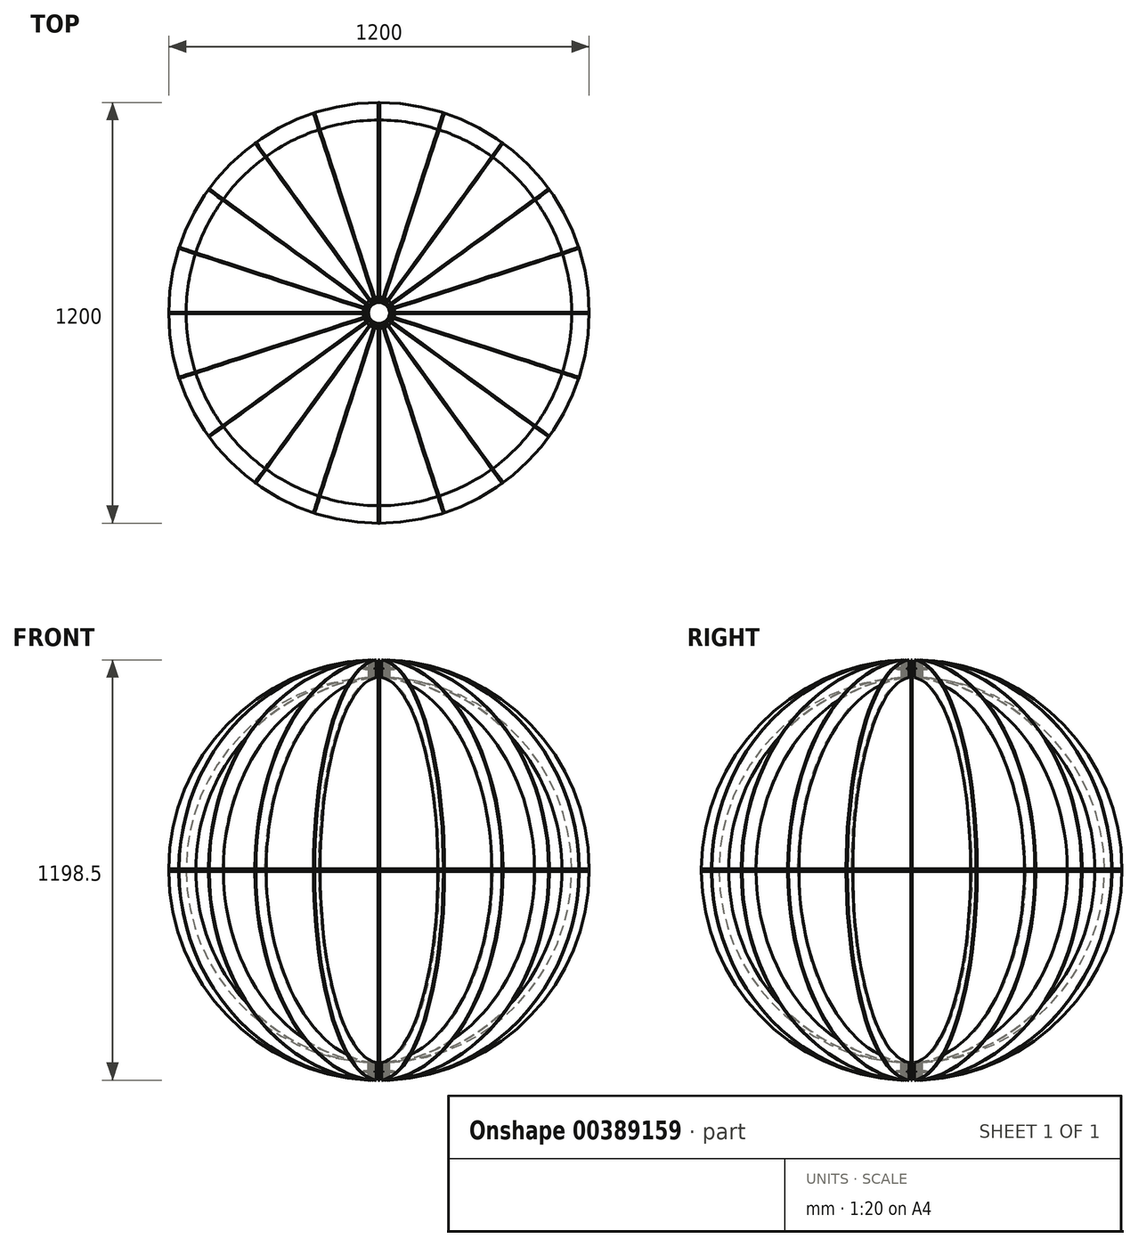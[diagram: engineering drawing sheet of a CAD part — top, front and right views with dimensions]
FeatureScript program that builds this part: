
annotation { "Feature Type Name" : "Feature", "Feature Type Description" : "" }
export const myFeature = defineFeature(function(context is Context, id is Id, definition is map)
    precondition{}
    {
        {
            var Q0;
            Q0=qCreatedBy(makeId("Front.planeOp"),FACE);
            var sketch = newSketch(context, id + "F0", { "sketchPlane" : qUnion([Q0])});
            skArc(sketch, "E0", {"start": v(-600, 0) * mm, "mid": v(-424.26, -424.26) * mm, "end": v(0, -600) * mm});
            skArc(sketch, "E1", {"start": v(-550, 0) * mm, "mid": v(-388.9, -388.9) * mm, "end": v(0, -550) * mm});
            skLineSegment(sketch, "E2", {"start": v(0, 0) * mm, "end": v(0, -799.31) * mm});
            skLineSegment(sketch, "E3", {"start": v(0, 0) * mm, "end": v(-999.51, 0) * mm});
            skLineSegment(sketch, "E4", {"start": v(-631.08, -4) * mm, "end": v(-585, -4) * mm});
            skLineSegment(sketch, "E5", {"start": v(-585, -4) * mm, "end": v(-585, -2) * mm});
            skLineSegment(sketch, "E6", {"start": v(-585, -2) * mm, "end": v(-565, -2) * mm});
            skLineSegment(sketch, "E7", {"start": v(-565, -2) * mm, "end": v(-565, -4) * mm});
            skLineSegment(sketch, "E8", {"start": v(-565, -4) * mm, "end": v(-518.76, -4) * mm});
            skLineSegment(sketch, "E9", {"start": v(-30, -645.62) * mm, "end": v(-30, -482.05) * mm});
            skLineSegment(sketch, "E10", {"start": v(-30, -577.5) * mm, "end": v(-40, -577.5) * mm});
            skLineSegment(sketch, "E11", {"start": v(-40, -577.5) * mm, "end": v(-40, -572.5) * mm});
            skLineSegment(sketch, "E12", {"start": v(-40, -572.5) * mm, "end": v(-30, -572.5) * mm});
            skSolve(sketch);
        }
        {
            var Q0;
            {var subQ12=sQuery(id+"F0.wireOp",EDGE,"E5");Q0=makeQuery(id+"F0.imprint","IMPRINT",FACE,{"disambiguationData":[TD([[makeQuery(id+"F0.imprint","IMPRINT",EDGE,{"derivedFrom":subQ12}),-1.0]])]});}
            extrude(context, id + "F1", {"entities" : qUnion([Q0]), "endBound" : BoundingType.SYMMETRIC, "depth" : 4 * mm});
        }
        {
            var Q0;
            Q0=qCreatedBy(makeId("Front.planeOp"),FACE);
            var sketch = newSketch(context, id + "F2", { "sketchPlane" : qUnion([Q0])});
            skLineSegment(sketch, "E13", {"start": v(0, -374.59) * mm, "end": v(0, 317) * mm});
            skSolve(sketch);
        }
        {
            var Q0;
            Q0=makeQuery(id+"F1.opExtrude","SWEPT_BODY",BODY,{"disambiguationData":[OSD([sQuery(id+"F0.wireOp",EDGE,"E0"),sQuery(id+"F0.wireOp",EDGE,"E1"),sQuery(id+"F0.wireOp",EDGE,"E4"),sQuery(id+"F0.wireOp",EDGE,"E5"),sQuery(id+"F0.wireOp",EDGE,"E6"),sQuery(id+"F0.wireOp",EDGE,"E7"),sQuery(id+"F0.wireOp",EDGE,"E8"),sQuery(id+"F0.wireOp",EDGE,"E9"),sQuery(id+"F0.wireOp",EDGE,"E10"),sQuery(id+"F0.wireOp",EDGE,"E11"),sQuery(id+"F0.wireOp",EDGE,"E12")])]});
            var Q1;
            Q1=sQuery(id+"F2.wireOp",EDGE,"E13");
            circularPattern(context, id + "F3", {"entities" : qUnion([Q0]), "axis" : qUnion([Q1]), "angle" : 360 * degree, "instanceCount" : 20, "equalSpace" : true});
        }
        {
            var Q0;
            Q0=qCreatedBy(makeId("Top.planeOp"),FACE);
            var sketch = newSketch(context, id + "F4", { "sketchPlane" : qUnion([Q0])});
            skLineSegment(sketch, "E14.0.0", {"start": v(-330.48, 458.27) * mm, "end": v(-342.24, 474.45) * mm});
            skLineSegment(sketch, "E14.0.1", {"start": v(-342.24, 474.45) * mm, "end": v(-345.47, 472.1) * mm});
            skLineSegment(sketch, "E14.0.2", {"start": v(-345.47, 472.1) * mm, "end": v(-333.72, 455.92) * mm});
            skLineSegment(sketch, "E14.0.3", {"start": v(-333.72, 455.92) * mm, "end": v(-330.48, 458.27) * mm});
            skLineSegment(sketch, "E15.0.0", {"start": v(-172.7, 537.96) * mm, "end": v(-178.87, 556.99) * mm});
            skLineSegment(sketch, "E15.0.1", {"start": v(-178.87, 556.99) * mm, "end": v(-182.68, 555.75) * mm});
            skLineSegment(sketch, "E15.0.2", {"start": v(-182.68, 555.75) * mm, "end": v(-176.5, 536.73) * mm});
            skLineSegment(sketch, "E15.0.3", {"start": v(-176.5, 536.73) * mm, "end": v(-172.7, 537.96) * mm});
            skLineSegment(sketch, "E16.0.0", {"start": v(2, 565) * mm, "end": v(2, 585) * mm});
            skLineSegment(sketch, "E16.0.1", {"start": v(2, 585) * mm, "end": v(-2, 585) * mm});
            skLineSegment(sketch, "E16.0.2", {"start": v(-2, 585) * mm, "end": v(-2, 565) * mm});
            skLineSegment(sketch, "E16.0.3", {"start": v(-2, 565) * mm, "end": v(2, 565) * mm});
            skLineSegment(sketch, "E17.0.0", {"start": v(176.5, 536.73) * mm, "end": v(182.68, 555.75) * mm});
            skLineSegment(sketch, "E17.0.1", {"start": v(182.68, 555.75) * mm, "end": v(178.87, 556.99) * mm});
            skLineSegment(sketch, "E17.0.2", {"start": v(178.87, 556.99) * mm, "end": v(172.7, 537.96) * mm});
            skLineSegment(sketch, "E17.0.3", {"start": v(172.7, 537.96) * mm, "end": v(176.5, 536.73) * mm});
            skLineSegment(sketch, "E18.0.0", {"start": v(333.72, 455.92) * mm, "end": v(345.47, 472.1) * mm});
            skLineSegment(sketch, "E18.0.1", {"start": v(345.47, 472.1) * mm, "end": v(342.24, 474.45) * mm});
            skLineSegment(sketch, "E18.0.2", {"start": v(342.24, 474.45) * mm, "end": v(330.48, 458.27) * mm});
            skLineSegment(sketch, "E18.0.3", {"start": v(330.48, 458.27) * mm, "end": v(333.72, 455.92) * mm});
            skLineSegment(sketch, "E19.0.0", {"start": v(458.27, 330.48) * mm, "end": v(474.45, 342.24) * mm});
            skLineSegment(sketch, "E19.0.1", {"start": v(474.45, 342.24) * mm, "end": v(472.1, 345.47) * mm});
            skLineSegment(sketch, "E19.0.2", {"start": v(472.1, 345.47) * mm, "end": v(455.92, 333.72) * mm});
            skLineSegment(sketch, "E19.0.3", {"start": v(455.92, 333.72) * mm, "end": v(458.27, 330.48) * mm});
            skLineSegment(sketch, "E20.0.0", {"start": v(537.96, 172.7) * mm, "end": v(556.99, 178.87) * mm});
            skLineSegment(sketch, "E20.0.1", {"start": v(556.99, 178.87) * mm, "end": v(555.75, 182.68) * mm});
            skLineSegment(sketch, "E20.0.2", {"start": v(555.75, 182.68) * mm, "end": v(536.73, 176.5) * mm});
            skLineSegment(sketch, "E20.0.3", {"start": v(536.73, 176.5) * mm, "end": v(537.96, 172.7) * mm});
            skLineSegment(sketch, "E21.0.0", {"start": v(565, -2) * mm, "end": v(585, -2) * mm});
            skLineSegment(sketch, "E21.0.1", {"start": v(585, -2) * mm, "end": v(585, 2) * mm});
            skLineSegment(sketch, "E21.0.2", {"start": v(585, 2) * mm, "end": v(565, 2) * mm});
            skLineSegment(sketch, "E21.0.3", {"start": v(565, 2) * mm, "end": v(565, -2) * mm});
            skLineSegment(sketch, "E22.0.0", {"start": v(536.73, -176.5) * mm, "end": v(555.75, -182.68) * mm});
            skLineSegment(sketch, "E22.0.1", {"start": v(555.75, -182.68) * mm, "end": v(556.99, -178.87) * mm});
            skLineSegment(sketch, "E22.0.2", {"start": v(556.99, -178.87) * mm, "end": v(537.96, -172.7) * mm});
            skLineSegment(sketch, "E22.0.3", {"start": v(537.96, -172.7) * mm, "end": v(536.73, -176.5) * mm});
            skLineSegment(sketch, "E23.0.0", {"start": v(455.92, -333.72) * mm, "end": v(472.1, -345.47) * mm});
            skLineSegment(sketch, "E23.0.1", {"start": v(472.1, -345.47) * mm, "end": v(474.45, -342.24) * mm});
            skLineSegment(sketch, "E23.0.2", {"start": v(474.45, -342.24) * mm, "end": v(458.27, -330.48) * mm});
            skLineSegment(sketch, "E23.0.3", {"start": v(458.27, -330.48) * mm, "end": v(455.92, -333.72) * mm});
            skLineSegment(sketch, "E24.0.0", {"start": v(330.48, -458.27) * mm, "end": v(342.24, -474.45) * mm});
            skLineSegment(sketch, "E24.0.1", {"start": v(342.24, -474.45) * mm, "end": v(345.47, -472.1) * mm});
            skLineSegment(sketch, "E24.0.2", {"start": v(345.47, -472.1) * mm, "end": v(333.72, -455.92) * mm});
            skLineSegment(sketch, "E24.0.3", {"start": v(333.72, -455.92) * mm, "end": v(330.48, -458.27) * mm});
            skLineSegment(sketch, "E25.0.0", {"start": v(172.7, -537.96) * mm, "end": v(178.87, -556.99) * mm});
            skLineSegment(sketch, "E25.0.1", {"start": v(178.87, -556.99) * mm, "end": v(182.68, -555.75) * mm});
            skLineSegment(sketch, "E25.0.2", {"start": v(182.68, -555.75) * mm, "end": v(176.5, -536.73) * mm});
            skLineSegment(sketch, "E25.0.3", {"start": v(176.5, -536.73) * mm, "end": v(172.7, -537.96) * mm});
            skLineSegment(sketch, "E26.0.0", {"start": v(-2, -565) * mm, "end": v(-2, -585) * mm});
            skLineSegment(sketch, "E26.0.1", {"start": v(-2, -585) * mm, "end": v(2, -585) * mm});
            skLineSegment(sketch, "E26.0.2", {"start": v(2, -585) * mm, "end": v(2, -565) * mm});
            skLineSegment(sketch, "E26.0.3", {"start": v(2, -565) * mm, "end": v(-2, -565) * mm});
            skLineSegment(sketch, "E27.0.0", {"start": v(-176.5, -536.73) * mm, "end": v(-182.68, -555.75) * mm});
            skLineSegment(sketch, "E27.0.1", {"start": v(-182.68, -555.75) * mm, "end": v(-178.87, -556.99) * mm});
            skLineSegment(sketch, "E27.0.2", {"start": v(-178.87, -556.99) * mm, "end": v(-172.7, -537.96) * mm});
            skLineSegment(sketch, "E27.0.3", {"start": v(-172.7, -537.96) * mm, "end": v(-176.5, -536.73) * mm});
            skLineSegment(sketch, "E28.0.0", {"start": v(-333.72, -455.92) * mm, "end": v(-345.47, -472.1) * mm});
            skLineSegment(sketch, "E28.0.1", {"start": v(-345.47, -472.1) * mm, "end": v(-342.24, -474.45) * mm});
            skLineSegment(sketch, "E28.0.2", {"start": v(-342.24, -474.45) * mm, "end": v(-330.48, -458.27) * mm});
            skLineSegment(sketch, "E28.0.3", {"start": v(-330.48, -458.27) * mm, "end": v(-333.72, -455.92) * mm});
            skLineSegment(sketch, "E29.0.0", {"start": v(-458.27, -330.48) * mm, "end": v(-474.45, -342.24) * mm});
            skLineSegment(sketch, "E29.0.1", {"start": v(-474.45, -342.24) * mm, "end": v(-472.1, -345.47) * mm});
            skLineSegment(sketch, "E29.0.2", {"start": v(-472.1, -345.47) * mm, "end": v(-455.92, -333.72) * mm});
            skLineSegment(sketch, "E29.0.3", {"start": v(-455.92, -333.72) * mm, "end": v(-458.27, -330.48) * mm});
            skLineSegment(sketch, "E30.0.0", {"start": v(-537.96, -172.7) * mm, "end": v(-556.99, -178.87) * mm});
            skLineSegment(sketch, "E30.0.1", {"start": v(-556.99, -178.87) * mm, "end": v(-555.75, -182.68) * mm});
            skLineSegment(sketch, "E30.0.2", {"start": v(-555.75, -182.68) * mm, "end": v(-536.73, -176.5) * mm});
            skLineSegment(sketch, "E30.0.3", {"start": v(-536.73, -176.5) * mm, "end": v(-537.96, -172.7) * mm});
            skLineSegment(sketch, "E31.0.0", {"start": v(-565, 2) * mm, "end": v(-585, 2) * mm});
            skLineSegment(sketch, "E31.0.1", {"start": v(-585, 2) * mm, "end": v(-585, -2) * mm});
            skLineSegment(sketch, "E31.0.2", {"start": v(-585, -2) * mm, "end": v(-565, -2) * mm});
            skLineSegment(sketch, "E31.0.3", {"start": v(-565, -2) * mm, "end": v(-565, 2) * mm});
            skLineSegment(sketch, "E32.0.0", {"start": v(-536.73, 176.5) * mm, "end": v(-555.75, 182.68) * mm});
            skLineSegment(sketch, "E32.0.1", {"start": v(-555.75, 182.68) * mm, "end": v(-556.99, 178.87) * mm});
            skLineSegment(sketch, "E32.0.2", {"start": v(-556.99, 178.87) * mm, "end": v(-537.96, 172.7) * mm});
            skLineSegment(sketch, "E32.0.3", {"start": v(-537.96, 172.7) * mm, "end": v(-536.73, 176.5) * mm});
            skLineSegment(sketch, "E33.0.0", {"start": v(-455.92, 333.72) * mm, "end": v(-472.1, 345.47) * mm});
            skLineSegment(sketch, "E33.0.1", {"start": v(-472.1, 345.47) * mm, "end": v(-474.45, 342.24) * mm});
            skLineSegment(sketch, "E33.0.2", {"start": v(-474.45, 342.24) * mm, "end": v(-458.27, 330.48) * mm});
            skLineSegment(sketch, "E33.0.3", {"start": v(-458.27, 330.48) * mm, "end": v(-455.92, 333.72) * mm});
            skCircle(sketch, "E34", {"center": v(0, 0) * mm, "radius": 600 * mm});
            skCircle(sketch, "E35", {"center": v(0, 0) * mm, "radius": 550 * mm});
            skSolve(sketch);
        }
        {
            var Q0;
            Q0=makeQuery(id+"F4.imprint","IMPRINT",FACE,{"disambiguationData":[TD([[makeQuery(id+"F4.imprint","IMPRINT",EDGE,{"derivedFrom":sQuery(id+"F4.wireOp",EDGE,"E14.0.0")}),-1.0]])]});
            extrude(context, id + "F5", {"entities" : qUnion([Q0]), "oppositeDirection" : true, "depth" : 4 * mm});
        }
        {
            var Q0;
            Q0=makeQuery(id+"F3.opPattern","COPY",FACE,{"derivedFrom":makeQuery(id+"F1.opExtrude","SWEPT_FACE",FACE,{"disambiguationData":[OSD([sQuery(id+"F0.wireOp",EDGE,"E12")])]}),"instanceName":"17"});
            var sketch = newSketch(context, id + "F6", { "sketchPlane" : qUnion([Q0])});
            skLineSegment(sketch, "E36.0.0", {"start": v(-31.19, -25.13) * mm, "end": v(-23.1, -19.25) * mm});
            skLineSegment(sketch, "E36.0.1", {"start": v(-23.1, -19.25) * mm, "end": v(-25.45, -16.02) * mm});
            skLineSegment(sketch, "E36.0.2", {"start": v(-25.45, -16.02) * mm, "end": v(-33.54, -21.9) * mm});
            skLineSegment(sketch, "E36.0.3", {"start": v(-33.54, -21.9) * mm, "end": v(-31.19, -25.13) * mm});
            skLineSegment(sketch, "E37.0.0", {"start": v(-37.42, -14.26) * mm, "end": v(-27.91, -11.17) * mm});
            skLineSegment(sketch, "E37.0.1", {"start": v(-27.91, -11.17) * mm, "end": v(-29.15, -7.37) * mm});
            skLineSegment(sketch, "E37.0.2", {"start": v(-29.15, -7.37) * mm, "end": v(-38.66, -10.46) * mm});
            skLineSegment(sketch, "E37.0.3", {"start": v(-38.66, -10.46) * mm, "end": v(-37.42, -14.26) * mm});
            skLineSegment(sketch, "E38.0.0", {"start": v(-10.46, -38.66) * mm, "end": v(-7.37, -29.15) * mm});
            skLineSegment(sketch, "E38.0.1", {"start": v(-7.37, -29.15) * mm, "end": v(-11.17, -27.91) * mm});
            skLineSegment(sketch, "E38.0.2", {"start": v(-11.17, -27.91) * mm, "end": v(-14.26, -37.42) * mm});
            skLineSegment(sketch, "E38.0.3", {"start": v(-14.26, -37.42) * mm, "end": v(-10.46, -38.66) * mm});
            skLineSegment(sketch, "E39.0.0", {"start": v(2, -40) * mm, "end": v(2, -30) * mm});
            skLineSegment(sketch, "E39.0.1", {"start": v(2, -30) * mm, "end": v(-2, -30) * mm});
            skLineSegment(sketch, "E39.0.2", {"start": v(-2, -30) * mm, "end": v(-2, -40) * mm});
            skLineSegment(sketch, "E39.0.3", {"start": v(-2, -40) * mm, "end": v(2, -40) * mm});
            skLineSegment(sketch, "E40.0.0", {"start": v(14.26, -37.42) * mm, "end": v(11.17, -27.91) * mm});
            skLineSegment(sketch, "E40.0.1", {"start": v(11.17, -27.91) * mm, "end": v(7.37, -29.15) * mm});
            skLineSegment(sketch, "E40.0.2", {"start": v(7.37, -29.15) * mm, "end": v(10.46, -38.66) * mm});
            skLineSegment(sketch, "E40.0.3", {"start": v(10.46, -38.66) * mm, "end": v(14.26, -37.42) * mm});
            skLineSegment(sketch, "E41.0", {"start": v(-25.13, -31.19) * mm, "end": v(-19.25, -23.1) * mm});
            skLineSegment(sketch, "E42.0", {"start": v(-25.13, -31.19) * mm, "end": v(-21.9, -33.54) * mm});
            skLineSegment(sketch, "E43.0", {"start": v(-21.9, -33.54) * mm, "end": v(-16.02, -25.45) * mm});
            skLineSegment(sketch, "E44.0", {"start": v(-19.25, -23.1) * mm, "end": v(-16.02, -25.45) * mm});
            skLineSegment(sketch, "E45.0.0", {"start": v(25.13, -31.19) * mm, "end": v(19.25, -23.1) * mm});
            skLineSegment(sketch, "E45.0.1", {"start": v(19.25, -23.1) * mm, "end": v(16.02, -25.45) * mm});
            skLineSegment(sketch, "E45.0.2", {"start": v(16.02, -25.45) * mm, "end": v(21.9, -33.54) * mm});
            skLineSegment(sketch, "E45.0.3", {"start": v(21.9, -33.54) * mm, "end": v(25.13, -31.19) * mm});
            skLineSegment(sketch, "E46.0.0", {"start": v(33.54, -21.9) * mm, "end": v(25.45, -16.02) * mm});
            skLineSegment(sketch, "E46.0.1", {"start": v(25.45, -16.02) * mm, "end": v(23.1, -19.25) * mm});
            skLineSegment(sketch, "E46.0.2", {"start": v(23.1, -19.25) * mm, "end": v(31.19, -25.13) * mm});
            skLineSegment(sketch, "E46.0.3", {"start": v(31.19, -25.13) * mm, "end": v(33.54, -21.9) * mm});
            skLineSegment(sketch, "E47.0.0", {"start": v(38.66, -10.46) * mm, "end": v(29.15, -7.37) * mm});
            skLineSegment(sketch, "E47.0.1", {"start": v(29.15, -7.37) * mm, "end": v(27.91, -11.17) * mm});
            skLineSegment(sketch, "E47.0.2", {"start": v(27.91, -11.17) * mm, "end": v(37.42, -14.26) * mm});
            skLineSegment(sketch, "E47.0.3", {"start": v(37.42, -14.26) * mm, "end": v(38.66, -10.46) * mm});
            skLineSegment(sketch, "E48.0.0", {"start": v(40, 2) * mm, "end": v(30, 2) * mm});
            skLineSegment(sketch, "E48.0.1", {"start": v(30, 2) * mm, "end": v(30, -2) * mm});
            skLineSegment(sketch, "E48.0.2", {"start": v(30, -2) * mm, "end": v(40, -2) * mm});
            skLineSegment(sketch, "E48.0.3", {"start": v(40, -2) * mm, "end": v(40, 2) * mm});
            skLineSegment(sketch, "E49.0.0", {"start": v(37.42, 14.26) * mm, "end": v(27.91, 11.17) * mm});
            skLineSegment(sketch, "E49.0.1", {"start": v(27.91, 11.17) * mm, "end": v(29.15, 7.37) * mm});
            skLineSegment(sketch, "E49.0.2", {"start": v(29.15, 7.37) * mm, "end": v(38.66, 10.46) * mm});
            skLineSegment(sketch, "E49.0.3", {"start": v(38.66, 10.46) * mm, "end": v(37.42, 14.26) * mm});
            skLineSegment(sketch, "E50.0.0", {"start": v(31.19, 25.13) * mm, "end": v(23.1, 19.25) * mm});
            skLineSegment(sketch, "E50.0.1", {"start": v(23.1, 19.25) * mm, "end": v(25.45, 16.02) * mm});
            skLineSegment(sketch, "E50.0.2", {"start": v(25.45, 16.02) * mm, "end": v(33.54, 21.9) * mm});
            skLineSegment(sketch, "E50.0.3", {"start": v(33.54, 21.9) * mm, "end": v(31.19, 25.13) * mm});
            skLineSegment(sketch, "E51.0.0", {"start": v(21.9, 33.54) * mm, "end": v(16.02, 25.45) * mm});
            skLineSegment(sketch, "E51.0.1", {"start": v(16.02, 25.45) * mm, "end": v(19.25, 23.1) * mm});
            skLineSegment(sketch, "E51.0.2", {"start": v(19.25, 23.1) * mm, "end": v(25.13, 31.19) * mm});
            skLineSegment(sketch, "E51.0.3", {"start": v(25.13, 31.19) * mm, "end": v(21.9, 33.54) * mm});
            skLineSegment(sketch, "E52.0.0", {"start": v(10.46, 38.66) * mm, "end": v(7.37, 29.15) * mm});
            skLineSegment(sketch, "E52.0.1", {"start": v(7.37, 29.15) * mm, "end": v(11.17, 27.91) * mm});
            skLineSegment(sketch, "E52.0.2", {"start": v(11.17, 27.91) * mm, "end": v(14.26, 37.42) * mm});
            skLineSegment(sketch, "E52.0.3", {"start": v(14.26, 37.42) * mm, "end": v(10.46, 38.66) * mm});
            skLineSegment(sketch, "E53.0.0", {"start": v(-2, 40) * mm, "end": v(-2, 30) * mm});
            skLineSegment(sketch, "E53.0.1", {"start": v(-2, 30) * mm, "end": v(2, 30) * mm});
            skLineSegment(sketch, "E53.0.2", {"start": v(2, 30) * mm, "end": v(2, 40) * mm});
            skLineSegment(sketch, "E53.0.3", {"start": v(2, 40) * mm, "end": v(-2, 40) * mm});
            skLineSegment(sketch, "E54.0.0", {"start": v(-14.26, 37.42) * mm, "end": v(-11.17, 27.91) * mm});
            skLineSegment(sketch, "E54.0.1", {"start": v(-11.17, 27.91) * mm, "end": v(-7.37, 29.15) * mm});
            skLineSegment(sketch, "E54.0.2", {"start": v(-7.37, 29.15) * mm, "end": v(-10.46, 38.66) * mm});
            skLineSegment(sketch, "E54.0.3", {"start": v(-10.46, 38.66) * mm, "end": v(-14.26, 37.42) * mm});
            skLineSegment(sketch, "E55.0.0", {"start": v(-25.13, 31.19) * mm, "end": v(-19.25, 23.1) * mm});
            skLineSegment(sketch, "E55.0.1", {"start": v(-19.25, 23.1) * mm, "end": v(-16.02, 25.45) * mm});
            skLineSegment(sketch, "E55.0.2", {"start": v(-16.02, 25.45) * mm, "end": v(-21.9, 33.54) * mm});
            skLineSegment(sketch, "E55.0.3", {"start": v(-21.9, 33.54) * mm, "end": v(-25.13, 31.19) * mm});
            skLineSegment(sketch, "E56.0.0", {"start": v(-33.54, 21.9) * mm, "end": v(-25.45, 16.02) * mm});
            skLineSegment(sketch, "E56.0.1", {"start": v(-25.45, 16.02) * mm, "end": v(-23.1, 19.25) * mm});
            skLineSegment(sketch, "E56.0.2", {"start": v(-23.1, 19.25) * mm, "end": v(-31.19, 25.13) * mm});
            skLineSegment(sketch, "E56.0.3", {"start": v(-31.19, 25.13) * mm, "end": v(-33.54, 21.9) * mm});
            skLineSegment(sketch, "E57.0.0", {"start": v(-38.66, 10.46) * mm, "end": v(-29.15, 7.37) * mm});
            skLineSegment(sketch, "E57.0.1", {"start": v(-29.15, 7.37) * mm, "end": v(-27.91, 11.17) * mm});
            skLineSegment(sketch, "E57.0.2", {"start": v(-27.91, 11.17) * mm, "end": v(-37.42, 14.26) * mm});
            skLineSegment(sketch, "E57.0.3", {"start": v(-37.42, 14.26) * mm, "end": v(-38.66, 10.46) * mm});
            skLineSegment(sketch, "E58.0.0", {"start": v(-40, -2) * mm, "end": v(-30, -2) * mm});
            skLineSegment(sketch, "E58.0.1", {"start": v(-30, -2) * mm, "end": v(-30, 2) * mm});
            skLineSegment(sketch, "E58.0.2", {"start": v(-30, 2) * mm, "end": v(-40, 2) * mm});
            skLineSegment(sketch, "E58.0.3", {"start": v(-40, 2) * mm, "end": v(-40, -2) * mm});
            skCircle(sketch, "E59", {"center": v(0, 0) * mm, "radius": 30 * mm});
            skArc(sketch, "E60", {"start": v(-15.8, 42.14) * mm, "mid": v(-20.43, 40.1) * mm, "end": v(-24.8, 37.55) * mm});
            skLineSegment(sketch, "E61", {"start": v(-2, 40) * mm, "end": v(-2, 44.96) * mm});
            skLineSegment(sketch, "E62", {"start": v(2, 40) * mm, "end": v(2, 44.96) * mm});
            skLineSegment(sketch, "E63", {"start": v(10.46, 38.66) * mm, "end": v(11.99, 43.37) * mm});
            skLineSegment(sketch, "E64", {"start": v(14.26, 37.42) * mm, "end": v(15.8, 42.14) * mm});
            skLineSegment(sketch, "E65", {"start": v(21.9, 33.54) * mm, "end": v(24.8, 37.55) * mm});
            skLineSegment(sketch, "E66", {"start": v(25.13, 31.19) * mm, "end": v(28.04, 35.2) * mm});
            skLineSegment(sketch, "E67", {"start": v(31.19, 25.13) * mm, "end": v(35.2, 28.04) * mm});
            skLineSegment(sketch, "E68", {"start": v(33.54, 21.9) * mm, "end": v(37.55, 24.8) * mm});
            skLineSegment(sketch, "E69", {"start": v(37.42, 14.26) * mm, "end": v(42.14, 15.8) * mm});
            skLineSegment(sketch, "E70", {"start": v(38.66, 10.46) * mm, "end": v(43.37, 11.99) * mm});
            skLineSegment(sketch, "E71", {"start": v(-14.26, 37.42) * mm, "end": v(-15.8, 42.14) * mm});
            skLineSegment(sketch, "E72", {"start": v(-10.46, 38.66) * mm, "end": v(-11.99, 43.37) * mm});
            skArc(sketch, "E73.trimOffspring", {"start": v(-2, 44.96) * mm, "mid": v(-7.04, 44.45) * mm, "end": v(-11.99, 43.37) * mm});
            skArc(sketch, "E74.trimOffspring", {"start": v(11.99, 43.37) * mm, "mid": v(7.04, 44.45) * mm, "end": v(2, 44.96) * mm});
            skArc(sketch, "E75.trimOffspring", {"start": v(24.8, 37.55) * mm, "mid": v(20.43, 40.1) * mm, "end": v(15.8, 42.14) * mm});
            skArc(sketch, "E76.trimOffspring", {"start": v(35.2, 28.04) * mm, "mid": v(31.82, 31.82) * mm, "end": v(28.04, 35.2) * mm});
            skArc(sketch, "E77.trimOffspring", {"start": v(42.14, 15.8) * mm, "mid": v(40.1, 20.43) * mm, "end": v(37.55, 24.8) * mm});
            skLineSegment(sketch, "E78", {"start": v(40, 2) * mm, "end": v(44.96, 2) * mm});
            skLineSegment(sketch, "E79", {"start": v(40, -2) * mm, "end": v(44.96, -2) * mm});
            skLineSegment(sketch, "E80", {"start": v(38.66, -10.46) * mm, "end": v(43.37, -11.99) * mm});
            skLineSegment(sketch, "E81", {"start": v(37.42, -14.26) * mm, "end": v(42.14, -15.8) * mm});
            skLineSegment(sketch, "E82", {"start": v(33.54, -21.9) * mm, "end": v(37.55, -24.8) * mm});
            skLineSegment(sketch, "E83", {"start": v(31.19, -25.13) * mm, "end": v(35.2, -28.04) * mm});
            skLineSegment(sketch, "E84", {"start": v(25.13, -31.19) * mm, "end": v(28.04, -35.2) * mm});
            skLineSegment(sketch, "E85", {"start": v(21.9, -33.54) * mm, "end": v(24.8, -37.55) * mm});
            skLineSegment(sketch, "E86", {"start": v(14.26, -37.42) * mm, "end": v(15.8, -42.14) * mm});
            skLineSegment(sketch, "E87", {"start": v(10.46, -38.66) * mm, "end": v(11.99, -43.37) * mm});
            skLineSegment(sketch, "E88", {"start": v(2, -40) * mm, "end": v(2, -44.96) * mm});
            skLineSegment(sketch, "E89", {"start": v(-2, -40) * mm, "end": v(-2, -44.96) * mm});
            skArc(sketch, "E90.trimOffspring", {"start": v(15.8, -42.14) * mm, "mid": v(20.43, -40.1) * mm, "end": v(24.8, -37.55) * mm});
            skArc(sketch, "E91.trimOffspring", {"start": v(28.04, -35.2) * mm, "mid": v(31.82, -31.82) * mm, "end": v(35.2, -28.04) * mm});
            skArc(sketch, "E92.trimOffspring", {"start": v(37.55, -24.8) * mm, "mid": v(40.1, -20.43) * mm, "end": v(42.14, -15.8) * mm});
            skArc(sketch, "E93.trimOffspring", {"start": v(43.37, -11.99) * mm, "mid": v(44.45, -7.04) * mm, "end": v(44.96, -2) * mm});
            skArc(sketch, "E94.trimOffspring", {"start": v(44.96, 2) * mm, "mid": v(44.45, 7.04) * mm, "end": v(43.37, 11.99) * mm});
            skArc(sketch, "E95.trimOffspring", {"start": v(2, -44.96) * mm, "mid": v(7.04, -44.45) * mm, "end": v(11.99, -43.37) * mm});
            skLineSegment(sketch, "E96", {"start": v(-10.46, -38.66) * mm, "end": v(-11.99, -43.37) * mm});
            skLineSegment(sketch, "E97", {"start": v(-14.26, -37.42) * mm, "end": v(-15.8, -42.14) * mm});
            skLineSegment(sketch, "E98", {"start": v(-21.9, -33.54) * mm, "end": v(-24.8, -37.55) * mm});
            skLineSegment(sketch, "E99", {"start": v(-25.13, -31.19) * mm, "end": v(-28.04, -35.2) * mm});
            skLineSegment(sketch, "E100", {"start": v(-31.19, -25.13) * mm, "end": v(-35.2, -28.04) * mm});
            skLineSegment(sketch, "E101", {"start": v(-33.54, -21.9) * mm, "end": v(-37.55, -24.8) * mm});
            skLineSegment(sketch, "E102", {"start": v(-37.42, -14.26) * mm, "end": v(-42.14, -15.8) * mm});
            skLineSegment(sketch, "E103", {"start": v(-38.66, -10.46) * mm, "end": v(-43.37, -11.99) * mm});
            skArc(sketch, "E104.trimOffspring", {"start": v(-42.14, -15.8) * mm, "mid": v(-40.1, -20.43) * mm, "end": v(-37.55, -24.8) * mm});
            skArc(sketch, "E105.trimOffspring", {"start": v(-35.2, -28.04) * mm, "mid": v(-31.82, -31.82) * mm, "end": v(-28.04, -35.2) * mm});
            skArc(sketch, "E106.trimOffspring", {"start": v(-24.8, -37.55) * mm, "mid": v(-20.43, -40.1) * mm, "end": v(-15.8, -42.14) * mm});
            skArc(sketch, "E107.trimOffspring", {"start": v(-11.99, -43.37) * mm, "mid": v(-7.04, -44.45) * mm, "end": v(-2, -44.96) * mm});
            skLineSegment(sketch, "E108", {"start": v(-40, -2) * mm, "end": v(-44.96, -2) * mm});
            skLineSegment(sketch, "E109", {"start": v(-40, 2) * mm, "end": v(-44.96, 2) * mm});
            skLineSegment(sketch, "E110", {"start": v(-38.66, 10.46) * mm, "end": v(-43.37, 11.99) * mm});
            skLineSegment(sketch, "E111", {"start": v(-37.42, 14.26) * mm, "end": v(-42.14, 15.8) * mm});
            skLineSegment(sketch, "E112", {"start": v(-33.54, 21.9) * mm, "end": v(-37.55, 24.8) * mm});
            skLineSegment(sketch, "E113", {"start": v(-31.19, 25.13) * mm, "end": v(-35.2, 28.04) * mm});
            skLineSegment(sketch, "E114", {"start": v(-25.13, 31.19) * mm, "end": v(-28.04, 35.2) * mm});
            skLineSegment(sketch, "E115", {"start": v(-21.9, 33.54) * mm, "end": v(-24.8, 37.55) * mm});
            skArc(sketch, "E116.trimOffspring", {"start": v(-44.96, -2) * mm, "mid": v(-44.45, -7.04) * mm, "end": v(-43.37, -11.99) * mm});
            skArc(sketch, "E117.trimOffspring", {"start": v(-43.37, 11.99) * mm, "mid": v(-44.45, 7.04) * mm, "end": v(-44.96, 2) * mm});
            skArc(sketch, "E118.trimOffspring", {"start": v(-37.55, 24.8) * mm, "mid": v(-40.1, 20.43) * mm, "end": v(-42.14, 15.8) * mm});
            skArc(sketch, "E119.trimOffspring", {"start": v(-28.04, 35.2) * mm, "mid": v(-31.82, 31.82) * mm, "end": v(-35.2, 28.04) * mm});
            skSolve(sketch);
        }
        {
            var Q0;
            Q0=qSketchRegion(id+"F6",true);
            extrude(context, id + "F7", {"entities" : qUnion([Q0]), "depth" : 4 * mm});
        }
        {
            var Q0;
            Q0=makeQuery(id+"F3.opPattern","COPY",BODY,{"derivedFrom":makeQuery(id+"F1.opExtrude","SWEPT_BODY",BODY,{"disambiguationData":[OSD([sQuery(id+"F0.wireOp",EDGE,"E0"),sQuery(id+"F0.wireOp",EDGE,"E1"),sQuery(id+"F0.wireOp",EDGE,"E4"),sQuery(id+"F0.wireOp",EDGE,"E5"),sQuery(id+"F0.wireOp",EDGE,"E6"),sQuery(id+"F0.wireOp",EDGE,"E7"),sQuery(id+"F0.wireOp",EDGE,"E8"),sQuery(id+"F0.wireOp",EDGE,"E9"),sQuery(id+"F0.wireOp",EDGE,"E10"),sQuery(id+"F0.wireOp",EDGE,"E11"),sQuery(id+"F0.wireOp",EDGE,"E12")])]}),"instanceName":"9"});
            var Q1;
            Q1=makeQuery(id+"F5.opExtrude","SWEPT_BODY",BODY,{"disambiguationData":[OSD([sQuery(id+"F4.wireOp",EDGE,"E14.0.0"),sQuery(id+"F4.wireOp",EDGE,"E14.0.1"),sQuery(id+"F4.wireOp",EDGE,"E14.0.2"),sQuery(id+"F4.wireOp",EDGE,"E14.0.3"),sQuery(id+"F4.wireOp",EDGE,"E15.0.0"),sQuery(id+"F4.wireOp",EDGE,"E15.0.1"),sQuery(id+"F4.wireOp",EDGE,"E15.0.2"),sQuery(id+"F4.wireOp",EDGE,"E15.0.3"),sQuery(id+"F4.wireOp",EDGE,"E16.0.0"),sQuery(id+"F4.wireOp",EDGE,"E16.0.1"),sQuery(id+"F4.wireOp",EDGE,"E16.0.2"),sQuery(id+"F4.wireOp",EDGE,"E16.0.3"),sQuery(id+"F4.wireOp",EDGE,"E17.0.0"),sQuery(id+"F4.wireOp",EDGE,"E17.0.1"),sQuery(id+"F4.wireOp",EDGE,"E17.0.2"),sQuery(id+"F4.wireOp",EDGE,"E17.0.3"),sQuery(id+"F4.wireOp",EDGE,"E18.0.0"),sQuery(id+"F4.wireOp",EDGE,"E18.0.1"),sQuery(id+"F4.wireOp",EDGE,"E18.0.2"),sQuery(id+"F4.wireOp",EDGE,"E18.0.3"),sQuery(id+"F4.wireOp",EDGE,"E19.0.0"),sQuery(id+"F4.wireOp",EDGE,"E19.0.1"),sQuery(id+"F4.wireOp",EDGE,"E19.0.2"),sQuery(id+"F4.wireOp",EDGE,"E19.0.3"),sQuery(id+"F4.wireOp",EDGE,"E20.0.0"),sQuery(id+"F4.wireOp",EDGE,"E20.0.1"),sQuery(id+"F4.wireOp",EDGE,"E20.0.2"),sQuery(id+"F4.wireOp",EDGE,"E20.0.3"),sQuery(id+"F4.wireOp",EDGE,"E21.0.0"),sQuery(id+"F4.wireOp",EDGE,"E21.0.1"),sQuery(id+"F4.wireOp",EDGE,"E21.0.2"),sQuery(id+"F4.wireOp",EDGE,"E21.0.3"),sQuery(id+"F4.wireOp",EDGE,"E22.0.0"),sQuery(id+"F4.wireOp",EDGE,"E22.0.1"),sQuery(id+"F4.wireOp",EDGE,"E22.0.2"),sQuery(id+"F4.wireOp",EDGE,"E22.0.3"),sQuery(id+"F4.wireOp",EDGE,"E23.0.0"),sQuery(id+"F4.wireOp",EDGE,"E23.0.1"),sQuery(id+"F4.wireOp",EDGE,"E23.0.2"),sQuery(id+"F4.wireOp",EDGE,"E23.0.3"),sQuery(id+"F4.wireOp",EDGE,"E24.0.0"),sQuery(id+"F4.wireOp",EDGE,"E24.0.1"),sQuery(id+"F4.wireOp",EDGE,"E24.0.2"),sQuery(id+"F4.wireOp",EDGE,"E24.0.3"),sQuery(id+"F4.wireOp",EDGE,"E25.0.0"),sQuery(id+"F4.wireOp",EDGE,"E25.0.1"),sQuery(id+"F4.wireOp",EDGE,"E25.0.2"),sQuery(id+"F4.wireOp",EDGE,"E25.0.3"),sQuery(id+"F4.wireOp",EDGE,"E26.0.0"),sQuery(id+"F4.wireOp",EDGE,"E26.0.1"),sQuery(id+"F4.wireOp",EDGE,"E26.0.2"),sQuery(id+"F4.wireOp",EDGE,"E26.0.3"),sQuery(id+"F4.wireOp",EDGE,"E27.0.0"),sQuery(id+"F4.wireOp",EDGE,"E27.0.1"),sQuery(id+"F4.wireOp",EDGE,"E27.0.2"),sQuery(id+"F4.wireOp",EDGE,"E27.0.3"),sQuery(id+"F4.wireOp",EDGE,"E28.0.0"),sQuery(id+"F4.wireOp",EDGE,"E28.0.1"),sQuery(id+"F4.wireOp",EDGE,"E28.0.2"),sQuery(id+"F4.wireOp",EDGE,"E28.0.3"),sQuery(id+"F4.wireOp",EDGE,"E29.0.0"),sQuery(id+"F4.wireOp",EDGE,"E29.0.1"),sQuery(id+"F4.wireOp",EDGE,"E29.0.2"),sQuery(id+"F4.wireOp",EDGE,"E29.0.3"),sQuery(id+"F4.wireOp",EDGE,"E30.0.0"),sQuery(id+"F4.wireOp",EDGE,"E30.0.1"),sQuery(id+"F4.wireOp",EDGE,"E30.0.2"),sQuery(id+"F4.wireOp",EDGE,"E30.0.3"),sQuery(id+"F4.wireOp",EDGE,"E31.0.0"),sQuery(id+"F4.wireOp",EDGE,"E31.0.1"),sQuery(id+"F4.wireOp",EDGE,"E31.0.2"),sQuery(id+"F4.wireOp",EDGE,"E31.0.3"),sQuery(id+"F4.wireOp",EDGE,"E32.0.0"),sQuery(id+"F4.wireOp",EDGE,"E32.0.1"),sQuery(id+"F4.wireOp",EDGE,"E32.0.2"),sQuery(id+"F4.wireOp",EDGE,"E32.0.3"),sQuery(id+"F4.wireOp",EDGE,"E33.0.0"),sQuery(id+"F4.wireOp",EDGE,"E33.0.1"),sQuery(id+"F4.wireOp",EDGE,"E33.0.2"),sQuery(id+"F4.wireOp",EDGE,"E33.0.3"),sQuery(id+"F4.wireOp",EDGE,"E34"),sQuery(id+"F4.wireOp",EDGE,"E35")])]});
            var Q2;
            Q2=makeQuery(id+"F3.opPattern","COPY",BODY,{"derivedFrom":makeQuery(id+"F1.opExtrude","SWEPT_BODY",BODY,{"disambiguationData":[OSD([sQuery(id+"F0.wireOp",EDGE,"E0"),sQuery(id+"F0.wireOp",EDGE,"E1"),sQuery(id+"F0.wireOp",EDGE,"E4"),sQuery(id+"F0.wireOp",EDGE,"E5"),sQuery(id+"F0.wireOp",EDGE,"E6"),sQuery(id+"F0.wireOp",EDGE,"E7"),sQuery(id+"F0.wireOp",EDGE,"E8"),sQuery(id+"F0.wireOp",EDGE,"E9"),sQuery(id+"F0.wireOp",EDGE,"E10"),sQuery(id+"F0.wireOp",EDGE,"E11"),sQuery(id+"F0.wireOp",EDGE,"E12")])]}),"instanceName":"15"});
            var Q3;
            Q3=makeQuery(id+"F3.opPattern","COPY",BODY,{"derivedFrom":makeQuery(id+"F1.opExtrude","SWEPT_BODY",BODY,{"disambiguationData":[OSD([sQuery(id+"F0.wireOp",EDGE,"E0"),sQuery(id+"F0.wireOp",EDGE,"E1"),sQuery(id+"F0.wireOp",EDGE,"E4"),sQuery(id+"F0.wireOp",EDGE,"E5"),sQuery(id+"F0.wireOp",EDGE,"E6"),sQuery(id+"F0.wireOp",EDGE,"E7"),sQuery(id+"F0.wireOp",EDGE,"E8"),sQuery(id+"F0.wireOp",EDGE,"E9"),sQuery(id+"F0.wireOp",EDGE,"E10"),sQuery(id+"F0.wireOp",EDGE,"E11"),sQuery(id+"F0.wireOp",EDGE,"E12")])]}),"instanceName":"17"});
            var Q4;
            Q4=makeQuery(id+"F3.opPattern","COPY",BODY,{"derivedFrom":makeQuery(id+"F1.opExtrude","SWEPT_BODY",BODY,{"disambiguationData":[OSD([sQuery(id+"F0.wireOp",EDGE,"E0"),sQuery(id+"F0.wireOp",EDGE,"E1"),sQuery(id+"F0.wireOp",EDGE,"E4"),sQuery(id+"F0.wireOp",EDGE,"E5"),sQuery(id+"F0.wireOp",EDGE,"E6"),sQuery(id+"F0.wireOp",EDGE,"E7"),sQuery(id+"F0.wireOp",EDGE,"E8"),sQuery(id+"F0.wireOp",EDGE,"E9"),sQuery(id+"F0.wireOp",EDGE,"E10"),sQuery(id+"F0.wireOp",EDGE,"E11"),sQuery(id+"F0.wireOp",EDGE,"E12")])]}),"instanceName":"11"});
            var Q5;
            Q5=makeQuery(id+"F3.opPattern","COPY",BODY,{"derivedFrom":makeQuery(id+"F1.opExtrude","SWEPT_BODY",BODY,{"disambiguationData":[OSD([sQuery(id+"F0.wireOp",EDGE,"E0"),sQuery(id+"F0.wireOp",EDGE,"E1"),sQuery(id+"F0.wireOp",EDGE,"E4"),sQuery(id+"F0.wireOp",EDGE,"E5"),sQuery(id+"F0.wireOp",EDGE,"E6"),sQuery(id+"F0.wireOp",EDGE,"E7"),sQuery(id+"F0.wireOp",EDGE,"E8"),sQuery(id+"F0.wireOp",EDGE,"E9"),sQuery(id+"F0.wireOp",EDGE,"E10"),sQuery(id+"F0.wireOp",EDGE,"E11"),sQuery(id+"F0.wireOp",EDGE,"E12")])]}),"instanceName":"2"});
            var Q6;
            Q6=makeQuery(id+"F3.opPattern","COPY",BODY,{"derivedFrom":makeQuery(id+"F1.opExtrude","SWEPT_BODY",BODY,{"disambiguationData":[OSD([sQuery(id+"F0.wireOp",EDGE,"E0"),sQuery(id+"F0.wireOp",EDGE,"E1"),sQuery(id+"F0.wireOp",EDGE,"E4"),sQuery(id+"F0.wireOp",EDGE,"E5"),sQuery(id+"F0.wireOp",EDGE,"E6"),sQuery(id+"F0.wireOp",EDGE,"E7"),sQuery(id+"F0.wireOp",EDGE,"E8"),sQuery(id+"F0.wireOp",EDGE,"E9"),sQuery(id+"F0.wireOp",EDGE,"E10"),sQuery(id+"F0.wireOp",EDGE,"E11"),sQuery(id+"F0.wireOp",EDGE,"E12")])]}),"instanceName":"19"});
            var Q7;
            Q7=makeQuery(id+"F3.opPattern","COPY",BODY,{"derivedFrom":makeQuery(id+"F1.opExtrude","SWEPT_BODY",BODY,{"disambiguationData":[OSD([sQuery(id+"F0.wireOp",EDGE,"E0"),sQuery(id+"F0.wireOp",EDGE,"E1"),sQuery(id+"F0.wireOp",EDGE,"E4"),sQuery(id+"F0.wireOp",EDGE,"E5"),sQuery(id+"F0.wireOp",EDGE,"E6"),sQuery(id+"F0.wireOp",EDGE,"E7"),sQuery(id+"F0.wireOp",EDGE,"E8"),sQuery(id+"F0.wireOp",EDGE,"E9"),sQuery(id+"F0.wireOp",EDGE,"E10"),sQuery(id+"F0.wireOp",EDGE,"E11"),sQuery(id+"F0.wireOp",EDGE,"E12")])]}),"instanceName":"14"});
            var Q8;
            Q8=makeQuery(id+"F3.opPattern","COPY",BODY,{"derivedFrom":makeQuery(id+"F1.opExtrude","SWEPT_BODY",BODY,{"disambiguationData":[OSD([sQuery(id+"F0.wireOp",EDGE,"E0"),sQuery(id+"F0.wireOp",EDGE,"E1"),sQuery(id+"F0.wireOp",EDGE,"E4"),sQuery(id+"F0.wireOp",EDGE,"E5"),sQuery(id+"F0.wireOp",EDGE,"E6"),sQuery(id+"F0.wireOp",EDGE,"E7"),sQuery(id+"F0.wireOp",EDGE,"E8"),sQuery(id+"F0.wireOp",EDGE,"E9"),sQuery(id+"F0.wireOp",EDGE,"E10"),sQuery(id+"F0.wireOp",EDGE,"E11"),sQuery(id+"F0.wireOp",EDGE,"E12")])]}),"instanceName":"3"});
            var Q9;
            Q9=makeQuery(id+"F3.opPattern","COPY",BODY,{"derivedFrom":makeQuery(id+"F1.opExtrude","SWEPT_BODY",BODY,{"disambiguationData":[OSD([sQuery(id+"F0.wireOp",EDGE,"E0"),sQuery(id+"F0.wireOp",EDGE,"E1"),sQuery(id+"F0.wireOp",EDGE,"E4"),sQuery(id+"F0.wireOp",EDGE,"E5"),sQuery(id+"F0.wireOp",EDGE,"E6"),sQuery(id+"F0.wireOp",EDGE,"E7"),sQuery(id+"F0.wireOp",EDGE,"E8"),sQuery(id+"F0.wireOp",EDGE,"E9"),sQuery(id+"F0.wireOp",EDGE,"E10"),sQuery(id+"F0.wireOp",EDGE,"E11"),sQuery(id+"F0.wireOp",EDGE,"E12")])]}),"instanceName":"10"});
            var Q10;
            Q10=makeQuery(id+"F7.opExtrude","SWEPT_BODY",BODY,{"disambiguationData":[OSD([sQuery(id+"F6.wireOp",EDGE,"E36.0.3"),sQuery(id+"F6.wireOp",EDGE,"E37.0.3"),sQuery(id+"F6.wireOp",EDGE,"E38.0.3"),sQuery(id+"F6.wireOp",EDGE,"E39.0.3"),sQuery(id+"F6.wireOp",EDGE,"E40.0.3"),sQuery(id+"F6.wireOp",EDGE,"E42.0"),sQuery(id+"F6.wireOp",EDGE,"E45.0.3"),sQuery(id+"F6.wireOp",EDGE,"E46.0.3"),sQuery(id+"F6.wireOp",EDGE,"E47.0.3"),sQuery(id+"F6.wireOp",EDGE,"E48.0.3"),sQuery(id+"F6.wireOp",EDGE,"E49.0.3"),sQuery(id+"F6.wireOp",EDGE,"E50.0.3"),sQuery(id+"F6.wireOp",EDGE,"E51.0.3"),sQuery(id+"F6.wireOp",EDGE,"E52.0.3"),sQuery(id+"F6.wireOp",EDGE,"E53.0.3"),sQuery(id+"F6.wireOp",EDGE,"E54.0.3"),sQuery(id+"F6.wireOp",EDGE,"E55.0.3"),sQuery(id+"F6.wireOp",EDGE,"E56.0.3"),sQuery(id+"F6.wireOp",EDGE,"E57.0.3"),sQuery(id+"F6.wireOp",EDGE,"E58.0.3"),sQuery(id+"F6.wireOp",EDGE,"E59"),sQuery(id+"F6.wireOp",EDGE,"E60"),sQuery(id+"F6.wireOp",EDGE,"E61"),sQuery(id+"F6.wireOp",EDGE,"E62"),sQuery(id+"F6.wireOp",EDGE,"E63"),sQuery(id+"F6.wireOp",EDGE,"E64"),sQuery(id+"F6.wireOp",EDGE,"E65"),sQuery(id+"F6.wireOp",EDGE,"E66"),sQuery(id+"F6.wireOp",EDGE,"E67"),sQuery(id+"F6.wireOp",EDGE,"E68"),sQuery(id+"F6.wireOp",EDGE,"E69"),sQuery(id+"F6.wireOp",EDGE,"E70"),sQuery(id+"F6.wireOp",EDGE,"E71"),sQuery(id+"F6.wireOp",EDGE,"E72"),sQuery(id+"F6.wireOp",EDGE,"E73.trimOffspring"),sQuery(id+"F6.wireOp",EDGE,"E74.trimOffspring"),sQuery(id+"F6.wireOp",EDGE,"E75.trimOffspring"),sQuery(id+"F6.wireOp",EDGE,"E76.trimOffspring"),sQuery(id+"F6.wireOp",EDGE,"E77.trimOffspring"),sQuery(id+"F6.wireOp",EDGE,"E78"),sQuery(id+"F6.wireOp",EDGE,"E79"),sQuery(id+"F6.wireOp",EDGE,"E80"),sQuery(id+"F6.wireOp",EDGE,"E81"),sQuery(id+"F6.wireOp",EDGE,"E82"),sQuery(id+"F6.wireOp",EDGE,"E83"),sQuery(id+"F6.wireOp",EDGE,"E84"),sQuery(id+"F6.wireOp",EDGE,"E85"),sQuery(id+"F6.wireOp",EDGE,"E86"),sQuery(id+"F6.wireOp",EDGE,"E87"),sQuery(id+"F6.wireOp",EDGE,"E88"),sQuery(id+"F6.wireOp",EDGE,"E89"),sQuery(id+"F6.wireOp",EDGE,"E90.trimOffspring"),sQuery(id+"F6.wireOp",EDGE,"E91.trimOffspring"),sQuery(id+"F6.wireOp",EDGE,"E92.trimOffspring"),sQuery(id+"F6.wireOp",EDGE,"E93.trimOffspring"),sQuery(id+"F6.wireOp",EDGE,"E94.trimOffspring"),sQuery(id+"F6.wireOp",EDGE,"E95.trimOffspring"),sQuery(id+"F6.wireOp",EDGE,"E96"),sQuery(id+"F6.wireOp",EDGE,"E97"),sQuery(id+"F6.wireOp",EDGE,"E98"),sQuery(id+"F6.wireOp",EDGE,"E99"),sQuery(id+"F6.wireOp",EDGE,"E100"),sQuery(id+"F6.wireOp",EDGE,"E101"),sQuery(id+"F6.wireOp",EDGE,"E102"),sQuery(id+"F6.wireOp",EDGE,"E103"),sQuery(id+"F6.wireOp",EDGE,"E104.trimOffspring"),sQuery(id+"F6.wireOp",EDGE,"E105.trimOffspring"),sQuery(id+"F6.wireOp",EDGE,"E106.trimOffspring"),sQuery(id+"F6.wireOp",EDGE,"E107.trimOffspring"),sQuery(id+"F6.wireOp",EDGE,"E108"),sQuery(id+"F6.wireOp",EDGE,"E109"),sQuery(id+"F6.wireOp",EDGE,"E110"),sQuery(id+"F6.wireOp",EDGE,"E111"),sQuery(id+"F6.wireOp",EDGE,"E112"),sQuery(id+"F6.wireOp",EDGE,"E113"),sQuery(id+"F6.wireOp",EDGE,"E114"),sQuery(id+"F6.wireOp",EDGE,"E115"),sQuery(id+"F6.wireOp",EDGE,"E116.trimOffspring"),sQuery(id+"F6.wireOp",EDGE,"E117.trimOffspring"),sQuery(id+"F6.wireOp",EDGE,"E118.trimOffspring"),sQuery(id+"F6.wireOp",EDGE,"E119.trimOffspring")])]});
            var Q11;
            Q11=makeQuery(id+"F3.opPattern","COPY",BODY,{"derivedFrom":makeQuery(id+"F1.opExtrude","SWEPT_BODY",BODY,{"disambiguationData":[OSD([sQuery(id+"F0.wireOp",EDGE,"E0"),sQuery(id+"F0.wireOp",EDGE,"E1"),sQuery(id+"F0.wireOp",EDGE,"E4"),sQuery(id+"F0.wireOp",EDGE,"E5"),sQuery(id+"F0.wireOp",EDGE,"E6"),sQuery(id+"F0.wireOp",EDGE,"E7"),sQuery(id+"F0.wireOp",EDGE,"E8"),sQuery(id+"F0.wireOp",EDGE,"E9"),sQuery(id+"F0.wireOp",EDGE,"E10"),sQuery(id+"F0.wireOp",EDGE,"E11"),sQuery(id+"F0.wireOp",EDGE,"E12")])]}),"instanceName":"7"});
            var Q12;
            Q12=makeQuery(id+"F3.opPattern","COPY",BODY,{"derivedFrom":makeQuery(id+"F1.opExtrude","SWEPT_BODY",BODY,{"disambiguationData":[OSD([sQuery(id+"F0.wireOp",EDGE,"E0"),sQuery(id+"F0.wireOp",EDGE,"E1"),sQuery(id+"F0.wireOp",EDGE,"E4"),sQuery(id+"F0.wireOp",EDGE,"E5"),sQuery(id+"F0.wireOp",EDGE,"E6"),sQuery(id+"F0.wireOp",EDGE,"E7"),sQuery(id+"F0.wireOp",EDGE,"E8"),sQuery(id+"F0.wireOp",EDGE,"E9"),sQuery(id+"F0.wireOp",EDGE,"E10"),sQuery(id+"F0.wireOp",EDGE,"E11"),sQuery(id+"F0.wireOp",EDGE,"E12")])]}),"instanceName":"8"});
            var Q13;
            Q13=makeQuery(id+"F3.opPattern","COPY",BODY,{"derivedFrom":makeQuery(id+"F1.opExtrude","SWEPT_BODY",BODY,{"disambiguationData":[OSD([sQuery(id+"F0.wireOp",EDGE,"E0"),sQuery(id+"F0.wireOp",EDGE,"E1"),sQuery(id+"F0.wireOp",EDGE,"E4"),sQuery(id+"F0.wireOp",EDGE,"E5"),sQuery(id+"F0.wireOp",EDGE,"E6"),sQuery(id+"F0.wireOp",EDGE,"E7"),sQuery(id+"F0.wireOp",EDGE,"E8"),sQuery(id+"F0.wireOp",EDGE,"E9"),sQuery(id+"F0.wireOp",EDGE,"E10"),sQuery(id+"F0.wireOp",EDGE,"E11"),sQuery(id+"F0.wireOp",EDGE,"E12")])]}),"instanceName":"6"});
            var Q14;
            Q14=makeQuery(id+"F3.opPattern","COPY",BODY,{"derivedFrom":makeQuery(id+"F1.opExtrude","SWEPT_BODY",BODY,{"disambiguationData":[OSD([sQuery(id+"F0.wireOp",EDGE,"E0"),sQuery(id+"F0.wireOp",EDGE,"E1"),sQuery(id+"F0.wireOp",EDGE,"E4"),sQuery(id+"F0.wireOp",EDGE,"E5"),sQuery(id+"F0.wireOp",EDGE,"E6"),sQuery(id+"F0.wireOp",EDGE,"E7"),sQuery(id+"F0.wireOp",EDGE,"E8"),sQuery(id+"F0.wireOp",EDGE,"E9"),sQuery(id+"F0.wireOp",EDGE,"E10"),sQuery(id+"F0.wireOp",EDGE,"E11"),sQuery(id+"F0.wireOp",EDGE,"E12")])]}),"instanceName":"5"});
            var Q15;
            Q15=makeQuery(id+"F3.opPattern","COPY",BODY,{"derivedFrom":makeQuery(id+"F1.opExtrude","SWEPT_BODY",BODY,{"disambiguationData":[OSD([sQuery(id+"F0.wireOp",EDGE,"E0"),sQuery(id+"F0.wireOp",EDGE,"E1"),sQuery(id+"F0.wireOp",EDGE,"E4"),sQuery(id+"F0.wireOp",EDGE,"E5"),sQuery(id+"F0.wireOp",EDGE,"E6"),sQuery(id+"F0.wireOp",EDGE,"E7"),sQuery(id+"F0.wireOp",EDGE,"E8"),sQuery(id+"F0.wireOp",EDGE,"E9"),sQuery(id+"F0.wireOp",EDGE,"E10"),sQuery(id+"F0.wireOp",EDGE,"E11"),sQuery(id+"F0.wireOp",EDGE,"E12")])]}),"instanceName":"13"});
            var Q16;
            Q16=makeQuery(id+"F3.opPattern","COPY",BODY,{"derivedFrom":makeQuery(id+"F1.opExtrude","SWEPT_BODY",BODY,{"disambiguationData":[OSD([sQuery(id+"F0.wireOp",EDGE,"E0"),sQuery(id+"F0.wireOp",EDGE,"E1"),sQuery(id+"F0.wireOp",EDGE,"E4"),sQuery(id+"F0.wireOp",EDGE,"E5"),sQuery(id+"F0.wireOp",EDGE,"E6"),sQuery(id+"F0.wireOp",EDGE,"E7"),sQuery(id+"F0.wireOp",EDGE,"E8"),sQuery(id+"F0.wireOp",EDGE,"E9"),sQuery(id+"F0.wireOp",EDGE,"E10"),sQuery(id+"F0.wireOp",EDGE,"E11"),sQuery(id+"F0.wireOp",EDGE,"E12")])]}),"instanceName":"16"});
            var Q17;
            Q17=makeQuery(id+"F3.opPattern","COPY",BODY,{"derivedFrom":makeQuery(id+"F1.opExtrude","SWEPT_BODY",BODY,{"disambiguationData":[OSD([sQuery(id+"F0.wireOp",EDGE,"E0"),sQuery(id+"F0.wireOp",EDGE,"E1"),sQuery(id+"F0.wireOp",EDGE,"E4"),sQuery(id+"F0.wireOp",EDGE,"E5"),sQuery(id+"F0.wireOp",EDGE,"E6"),sQuery(id+"F0.wireOp",EDGE,"E7"),sQuery(id+"F0.wireOp",EDGE,"E8"),sQuery(id+"F0.wireOp",EDGE,"E9"),sQuery(id+"F0.wireOp",EDGE,"E10"),sQuery(id+"F0.wireOp",EDGE,"E11"),sQuery(id+"F0.wireOp",EDGE,"E12")])]}),"instanceName":"12"});
            var Q18;
            Q18=makeQuery(id+"F3.opPattern","COPY",BODY,{"derivedFrom":makeQuery(id+"F1.opExtrude","SWEPT_BODY",BODY,{"disambiguationData":[OSD([sQuery(id+"F0.wireOp",EDGE,"E0"),sQuery(id+"F0.wireOp",EDGE,"E1"),sQuery(id+"F0.wireOp",EDGE,"E4"),sQuery(id+"F0.wireOp",EDGE,"E5"),sQuery(id+"F0.wireOp",EDGE,"E6"),sQuery(id+"F0.wireOp",EDGE,"E7"),sQuery(id+"F0.wireOp",EDGE,"E8"),sQuery(id+"F0.wireOp",EDGE,"E9"),sQuery(id+"F0.wireOp",EDGE,"E10"),sQuery(id+"F0.wireOp",EDGE,"E11"),sQuery(id+"F0.wireOp",EDGE,"E12")])]}),"instanceName":"4"});
            var Q19;
            Q19=makeQuery(id+"F3.opPattern","COPY",BODY,{"derivedFrom":makeQuery(id+"F1.opExtrude","SWEPT_BODY",BODY,{"disambiguationData":[OSD([sQuery(id+"F0.wireOp",EDGE,"E0"),sQuery(id+"F0.wireOp",EDGE,"E1"),sQuery(id+"F0.wireOp",EDGE,"E4"),sQuery(id+"F0.wireOp",EDGE,"E5"),sQuery(id+"F0.wireOp",EDGE,"E6"),sQuery(id+"F0.wireOp",EDGE,"E7"),sQuery(id+"F0.wireOp",EDGE,"E8"),sQuery(id+"F0.wireOp",EDGE,"E9"),sQuery(id+"F0.wireOp",EDGE,"E10"),sQuery(id+"F0.wireOp",EDGE,"E11"),sQuery(id+"F0.wireOp",EDGE,"E12")])]}),"instanceName":"18"});
            var Q20;
            Q20=makeQuery(id+"F3.opPattern","COPY",BODY,{"derivedFrom":makeQuery(id+"F1.opExtrude","SWEPT_BODY",BODY,{"disambiguationData":[OSD([sQuery(id+"F0.wireOp",EDGE,"E0"),sQuery(id+"F0.wireOp",EDGE,"E1"),sQuery(id+"F0.wireOp",EDGE,"E4"),sQuery(id+"F0.wireOp",EDGE,"E5"),sQuery(id+"F0.wireOp",EDGE,"E6"),sQuery(id+"F0.wireOp",EDGE,"E7"),sQuery(id+"F0.wireOp",EDGE,"E8"),sQuery(id+"F0.wireOp",EDGE,"E9"),sQuery(id+"F0.wireOp",EDGE,"E10"),sQuery(id+"F0.wireOp",EDGE,"E11"),sQuery(id+"F0.wireOp",EDGE,"E12")])]}),"instanceName":"1"});
            var Q21;
            Q21=makeQuery(id+"F1.opExtrude","SWEPT_BODY",BODY,{"disambiguationData":[OSD([sQuery(id+"F0.wireOp",EDGE,"E0"),sQuery(id+"F0.wireOp",EDGE,"E1"),sQuery(id+"F0.wireOp",EDGE,"E4"),sQuery(id+"F0.wireOp",EDGE,"E5"),sQuery(id+"F0.wireOp",EDGE,"E6"),sQuery(id+"F0.wireOp",EDGE,"E7"),sQuery(id+"F0.wireOp",EDGE,"E8"),sQuery(id+"F0.wireOp",EDGE,"E9"),sQuery(id+"F0.wireOp",EDGE,"E10"),sQuery(id+"F0.wireOp",EDGE,"E11"),sQuery(id+"F0.wireOp",EDGE,"E12")])]});
            var Q22;
            Q22=qCreatedBy(makeId("Top.planeOp"),FACE);
            mirror(context, id + "F8", {"entities" : qUnion([Q0, Q1, Q2, Q3, Q4, Q5, Q6, Q7, Q8, Q9, Q10, Q11, Q12, Q13, Q14, Q15, Q16, Q17, Q18, Q19, Q20, Q21]), "mirrorPlane" : qUnion([Q22])});
        }
    });
